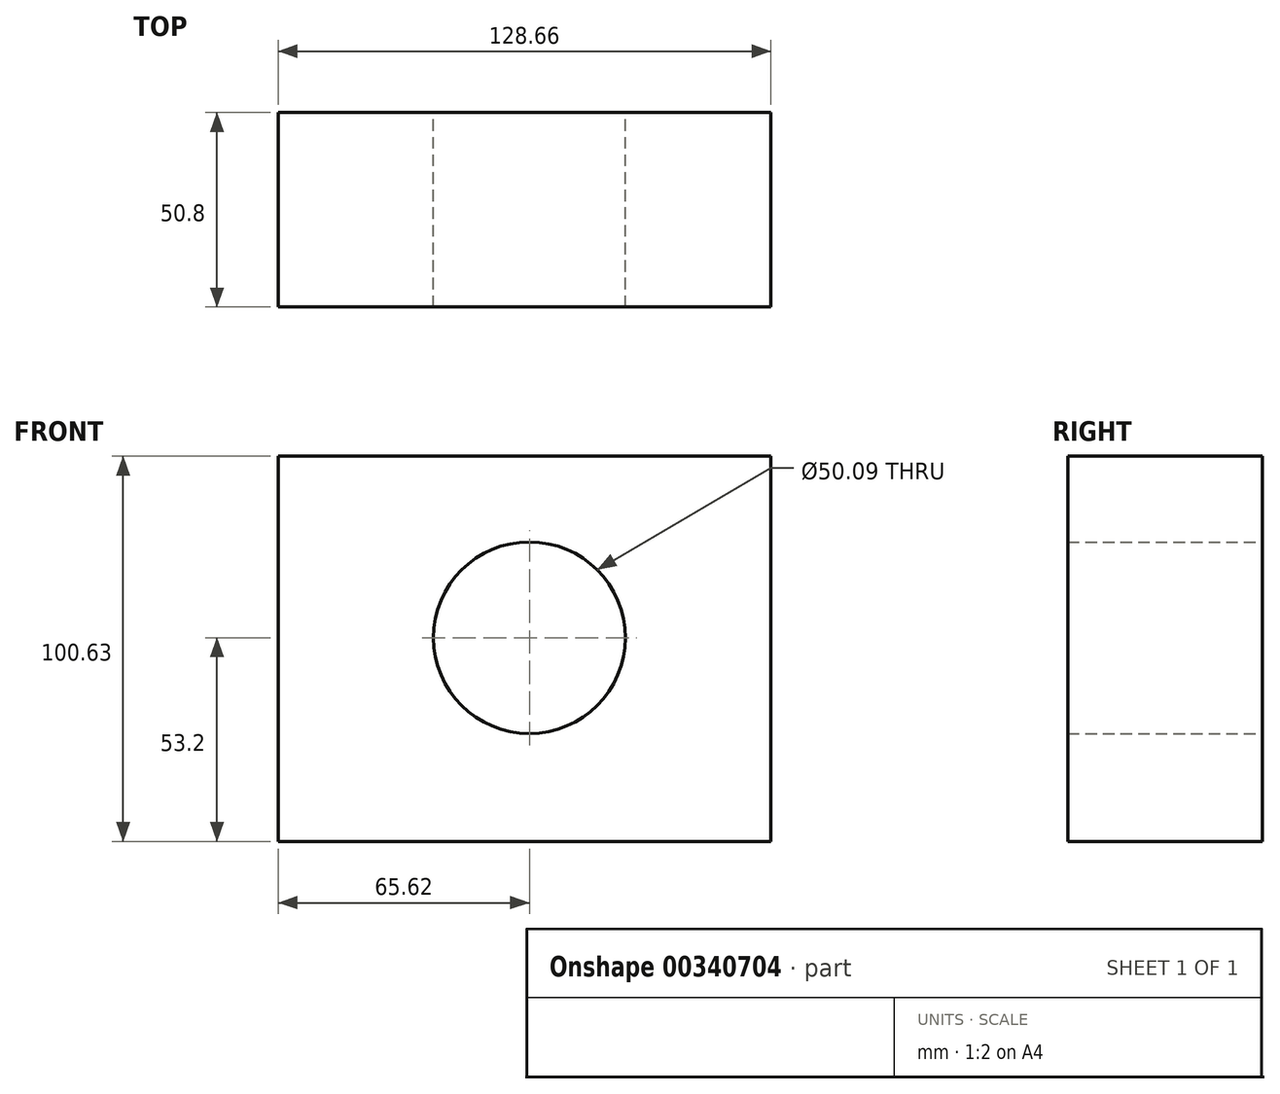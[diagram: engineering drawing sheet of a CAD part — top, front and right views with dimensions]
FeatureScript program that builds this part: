
annotation { "Feature Type Name" : "Feature", "Feature Type Description" : "" }
export const myFeature = defineFeature(function(context is Context, id is Id, definition is map)
    precondition{}
    {
        {
            var Q0;
            Q0=qCreatedBy(makeId("Front.planeOp"),FACE);
            var sketch = newSketch(context, id + "F0", { "sketchPlane" : qUnion([Q0])});
            skLineSegment(sketch, "E0.bottom", {"start": v(-65.62, 47.43) * mm, "end": v(63.04, 47.43) * mm});
            skLineSegment(sketch, "E0.top", {"start": v(-65.62, -53.2) * mm, "end": v(63.04, -53.2) * mm});
            skLineSegment(sketch, "E0.left", {"start": v(-65.62, 47.43) * mm, "end": v(-65.62, -53.2) * mm});
            skLineSegment(sketch, "E0.right", {"start": v(63.04, 47.43) * mm, "end": v(63.04, -53.2) * mm});
            skCircle(sketch, "E1", {"center": v(0, 0) * mm, "radius": 25.04 * mm});
            skSolve(sketch);
        }
        {
            var Q0;
            Q0=makeQuery(id+"F0.imprint","IMPRINT",FACE,{"disambiguationData":[TD([[makeQuery(id+"F0.imprint","IMPRINT",EDGE,{"derivedFrom":sQuery(id+"F0.wireOp",EDGE,"E0.bottom")}),-1.0]])]});
            extrude(context, id + "F1", {"entities" : qUnion([Q0]), "depth" : 50.8 * mm});
        }
        {
            var Q0;
            Q0=qCreatedBy(makeId("Front.planeOp"),FACE);
            var sketch = newSketch(context, id + "F2", { "sketchPlane" : qUnion([Q0])});
            skCircle(sketch, "E2", {"center": v(0, 0) * mm, "radius": 31 * mm});
            skSolve(sketch);
        }
        {
            var Q0;
            Q0=sQuery(id+"F2.wireOp",EDGE,"E2");
            extrude(context, id + "F3", {"bodyType" : ToolBodyType.SURFACE, "operationType" : NewBodyOperationType.INTERSECT, "surfaceEntities" : qUnion([Q0]), "depth" : 76.45 * mm});
        }
    });
